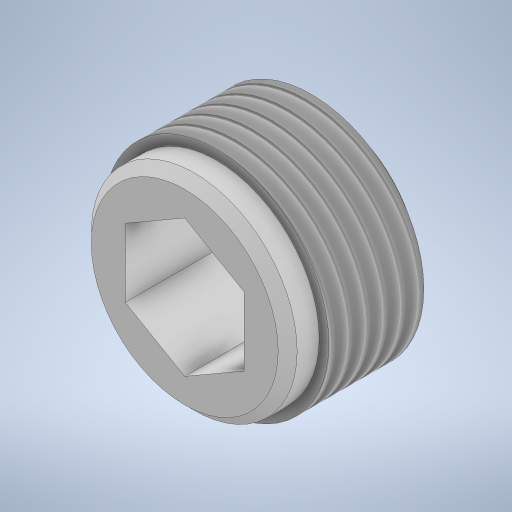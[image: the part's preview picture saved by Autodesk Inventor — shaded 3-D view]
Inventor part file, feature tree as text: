
AUTODESK INVENTOR PART (.ipt)
format: ipt  version: 2024 (Build 280153000, 153)  size: 329,216 bytes
history: native  units: in
note: dims shown in document units (in); Inventor stores cm internally (conversion verified against a paired STEP export)
features: extrude x5, sketch x5, projected_geometry x2, chamfer x1, thread x1, mirror x1
ambient origin geometry x8: Origin, YZ Plane, XZ Plane, XY Plane, X Axis, Y Axis, Z Axis, Center Point
bodies: Solid1 (feature_tree), Solid2 (feature_tree)
feature tree (15):
  extrude  "Extrusion1"  Depth=0.2in TaperAngle=0.0deg
  extrude  "Extrusion2"  Depth=0.025in
  extrude  "Extrusion3"  Depth=0.05in TaperAngle=0.0deg
  chamfer  "Chamfer1"  Distance=0.015in Angle=45.0deg
  extrude  "Extrusion4"  Depth=0.15in TaperAngle=0.0deg
  thread  "Thread1"  [1 undecoded]
  mirror  "Mirror1"
  extrude  "Extrusion5"  [1 undecoded]
  sketch  "Sketch1"  dims[d0=0.355in d1=0.2in d2=0.0in]
  sketch  "Sketch2"  dims[d3=0.3in d4=0.025in d5=-0.1031in]
  sketch  "Sketch3"  dims[d6=0.325in d7=0.05in d8=0.0in d9=0.015in d10=0.125in d11=45.0deg]
  projected_geometry  "Projected Loop1"
  sketch  "Sketch4"  dims[d12=0.1875in d13=100.0in d14=0.0in d15=0.15in d16=0.0in]
  sketch  "Sketch6"  dims[d17=0.25in d18=0.0in]
  projected_geometry  "Project Cut Edges1"
note: 2 required parameter values undecoded (feature->parameter linkage not recoverable at this tier; creation-order binding heuristic only, values carry confidence <= 0.55)
